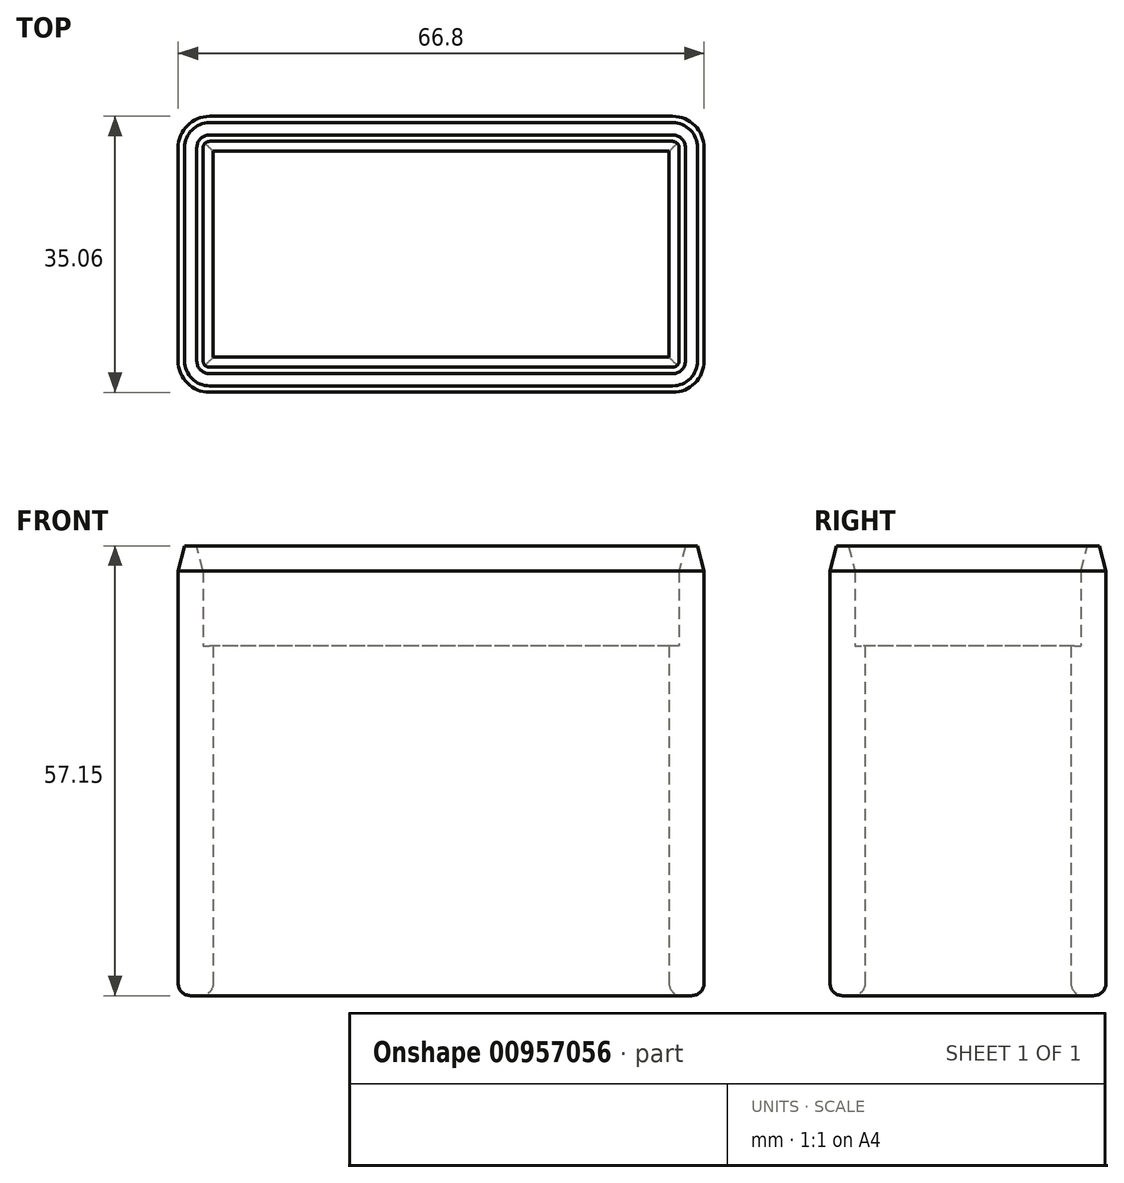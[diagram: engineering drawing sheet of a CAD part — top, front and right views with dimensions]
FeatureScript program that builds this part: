
annotation { "Feature Type Name" : "Feature", "Feature Type Description" : "" }
export const myFeature = defineFeature(function(context is Context, id is Id, definition is map)
    precondition{}
    {
        {
            var Q0;
            Q0=qCreatedBy(makeId("Top.planeOp"),FACE);
            var sketch = newSketch(context, id + "F0", { "sketchPlane" : qUnion([Q0])});
            skLineSegment(sketch, "E0.bottom", {"start": v(29.41, 14.35) * mm, "end": v(-29.41, 14.35) * mm});
            skLineSegment(sketch, "E0.top", {"start": v(29.41, -14.35) * mm, "end": v(-29.41, -14.35) * mm});
            skLineSegment(sketch, "E0.left", {"start": v(30.23, 13.54) * mm, "end": v(30.23, -13.54) * mm});
            skLineSegment(sketch, "E0.right", {"start": v(-30.23, 13.54) * mm, "end": v(-30.23, -13.54) * mm});
            skPoint(sketch, "E0.middle", {"position": v(0, 0) * mm});
            skPoint(sketch, "E1.visualSharp", {"position": v(-30.23, 14.35) * mm});
            skArc(sketch, "E1.filletArc", {"start": v(-29.41, 14.35) * mm, "mid": v(-29.99, 14.11) * mm, "end": v(-30.23, 13.54) * mm});
            skPoint(sketch, "E2.visualSharp", {"position": v(30.23, 14.35) * mm});
            skArc(sketch, "E2.filletArc", {"start": v(30.23, 13.54) * mm, "mid": v(29.99, 14.11) * mm, "end": v(29.41, 14.35) * mm});
            skPoint(sketch, "E3.visualSharp", {"position": v(30.23, -14.35) * mm});
            skArc(sketch, "E3.filletArc", {"start": v(29.41, -14.35) * mm, "mid": v(29.99, -14.11) * mm, "end": v(30.23, -13.54) * mm});
            skPoint(sketch, "E4.visualSharp", {"position": v(-30.23, -14.35) * mm});
            skArc(sketch, "E4.filletArc", {"start": v(-30.23, -13.54) * mm, "mid": v(-29.99, -14.11) * mm, "end": v(-29.41, -14.35) * mm});
            skArc(sketch, "E5.0", {"start": v(-29.41, 17.53) * mm, "mid": v(-32.23, 16.36) * mm, "end": v(-33.4, 13.54) * mm});
            skLineSegment(sketch, "E5.1", {"start": v(29.41, 17.53) * mm, "end": v(-29.41, 17.53) * mm});
            skLineSegment(sketch, "E5.2", {"start": v(-33.4, 13.54) * mm, "end": v(-33.4, -13.54) * mm});
            skArc(sketch, "E5.3", {"start": v(33.4, 13.54) * mm, "mid": v(32.23, 16.36) * mm, "end": v(29.41, 17.53) * mm});
            skArc(sketch, "E5.4", {"start": v(-33.4, -13.54) * mm, "mid": v(-32.23, -16.36) * mm, "end": v(-29.41, -17.53) * mm});
            skLineSegment(sketch, "E5.5", {"start": v(29.41, -17.53) * mm, "end": v(-29.41, -17.53) * mm});
            skArc(sketch, "E5.6", {"start": v(29.41, -17.53) * mm, "mid": v(32.23, -16.36) * mm, "end": v(33.4, -13.54) * mm});
            skLineSegment(sketch, "E5.7", {"start": v(33.4, 13.54) * mm, "end": v(33.4, -13.54) * mm});
            skLineSegment(sketch, "E6.0", {"start": v(28.96, 13.08) * mm, "end": v(-28.96, 13.08) * mm});
            skLineSegment(sketch, "E6.1", {"start": v(28.96, 13.08) * mm, "end": v(28.96, -13.08) * mm});
            skLineSegment(sketch, "E6.2", {"start": v(28.96, -13.08) * mm, "end": v(-28.96, -13.08) * mm});
            skLineSegment(sketch, "E6.3", {"start": v(-28.96, 13.08) * mm, "end": v(-28.96, -13.08) * mm});
            skSolve(sketch);
        }
        {
            var Q0;
            Q0=makeQuery(id+"F0.imprint","IMPRINT",FACE,{"disambiguationData":[TD([[makeQuery(id+"F0.imprint","IMPRINT",EDGE,{"derivedFrom":sQuery(id+"F0.wireOp",EDGE,"E0.bottom")}),-1.0]])]});
            extrude(context, id + "F1", {"entities" : qUnion([Q0]), "depth" : 57.15 * mm, "offsetDistance" : 25.4 * mm});
        }
        {
            var Q0;
            Q0=makeQuery(id+"F0.imprint","IMPRINT",FACE,{"disambiguationData":[TD([[makeQuery(id+"F0.imprint","IMPRINT",EDGE,{"derivedFrom":sQuery(id+"F0.wireOp",EDGE,"E0.bottom")}),1.0]])]});
            extrude(context, id + "F2", {"entities" : qUnion([Q0]), "operationType" : NewBodyOperationType.ADD, "depth" : 44.45 * mm, "offsetDistance" : 25.4 * mm});
        }
        {
            var Q0;
            Q0=makeQuery(id+"F1.opExtrude","CAP_FACE",FACE,{"disambiguationData":[OSD([sQuery(id+"F0.wireOp",EDGE,"E0.bottom"),sQuery(id+"F0.wireOp",EDGE,"E0.top"),sQuery(id+"F0.wireOp",EDGE,"E0.left"),sQuery(id+"F0.wireOp",EDGE,"E0.right"),sQuery(id+"F0.wireOp",EDGE,"E1.filletArc"),sQuery(id+"F0.wireOp",EDGE,"E2.filletArc"),sQuery(id+"F0.wireOp",EDGE,"E3.filletArc"),sQuery(id+"F0.wireOp",EDGE,"E4.filletArc"),sQuery(id+"F0.wireOp",EDGE,"E5.0"),sQuery(id+"F0.wireOp",EDGE,"E5.1"),sQuery(id+"F0.wireOp",EDGE,"E5.2"),sQuery(id+"F0.wireOp",EDGE,"E5.3"),sQuery(id+"F0.wireOp",EDGE,"E5.4"),sQuery(id+"F0.wireOp",EDGE,"E5.5"),sQuery(id+"F0.wireOp",EDGE,"E5.6"),sQuery(id+"F0.wireOp",EDGE,"E5.7")])],"isStart":false});
            chamfer(context, id + "F3", {"entities" : qUnion([Q0]), "chamferType" : ChamferType.TWO_OFFSETS, "width1" : 3.17 * mm, "oppositeDirection" : false, "width2" : 0.81 * mm, "tangentPropagation" : true});
        }
        {
            var Q0;
            {var subQ0=sQuery(id+"F0.wireOp",EDGE,"E4.filletArc");var subQ1=sQuery(id+"F0.wireOp",EDGE,"E3.filletArc");var subQ2=sQuery(id+"F0.wireOp",EDGE,"E2.filletArc");var subQ3=sQuery(id+"F0.wireOp",EDGE,"E1.filletArc");var subQ4=sQuery(id+"F0.wireOp",EDGE,"E0.right");var subQ5=sQuery(id+"F0.wireOp",EDGE,"E0.left");var subQ6=sQuery(id+"F0.wireOp",EDGE,"E0.top");var subQ7=sQuery(id+"F0.wireOp",EDGE,"E0.bottom");Q0=makeQuery(id+"F2.boolean.opBoolean","MERGE",FACE,{"derivedFrom":[makeQuery(id+"F1.opExtrude","CAP_FACE",FACE,{"disambiguationData":[OSD([subQ7,subQ6,subQ5,subQ4,subQ3,subQ2,subQ1,subQ0,sQuery(id+"F0.wireOp",EDGE,"E5.0"),sQuery(id+"F0.wireOp",EDGE,"E5.1"),sQuery(id+"F0.wireOp",EDGE,"E5.2"),sQuery(id+"F0.wireOp",EDGE,"E5.3"),sQuery(id+"F0.wireOp",EDGE,"E5.4"),sQuery(id+"F0.wireOp",EDGE,"E5.5"),sQuery(id+"F0.wireOp",EDGE,"E5.6"),sQuery(id+"F0.wireOp",EDGE,"E5.7")])],"isStart":true}),makeQuery(id+"F2.opExtrude","CAP_FACE",FACE,{"disambiguationData":[OSD([subQ7,subQ6,subQ5,subQ4,subQ3,subQ2,subQ1,subQ0,sQuery(id+"F0.wireOp",EDGE,"E6.0"),sQuery(id+"F0.wireOp",EDGE,"E6.1"),sQuery(id+"F0.wireOp",EDGE,"E6.2"),sQuery(id+"F0.wireOp",EDGE,"E6.3")])],"isStart":true})]});}
            fillet(context, id + "F4", {"entities" : qUnion([Q0]), "radius" : 1.57 * mm, "tangentPropagation" : true, "allowEdgeOverflow" : false});
        }
    });
